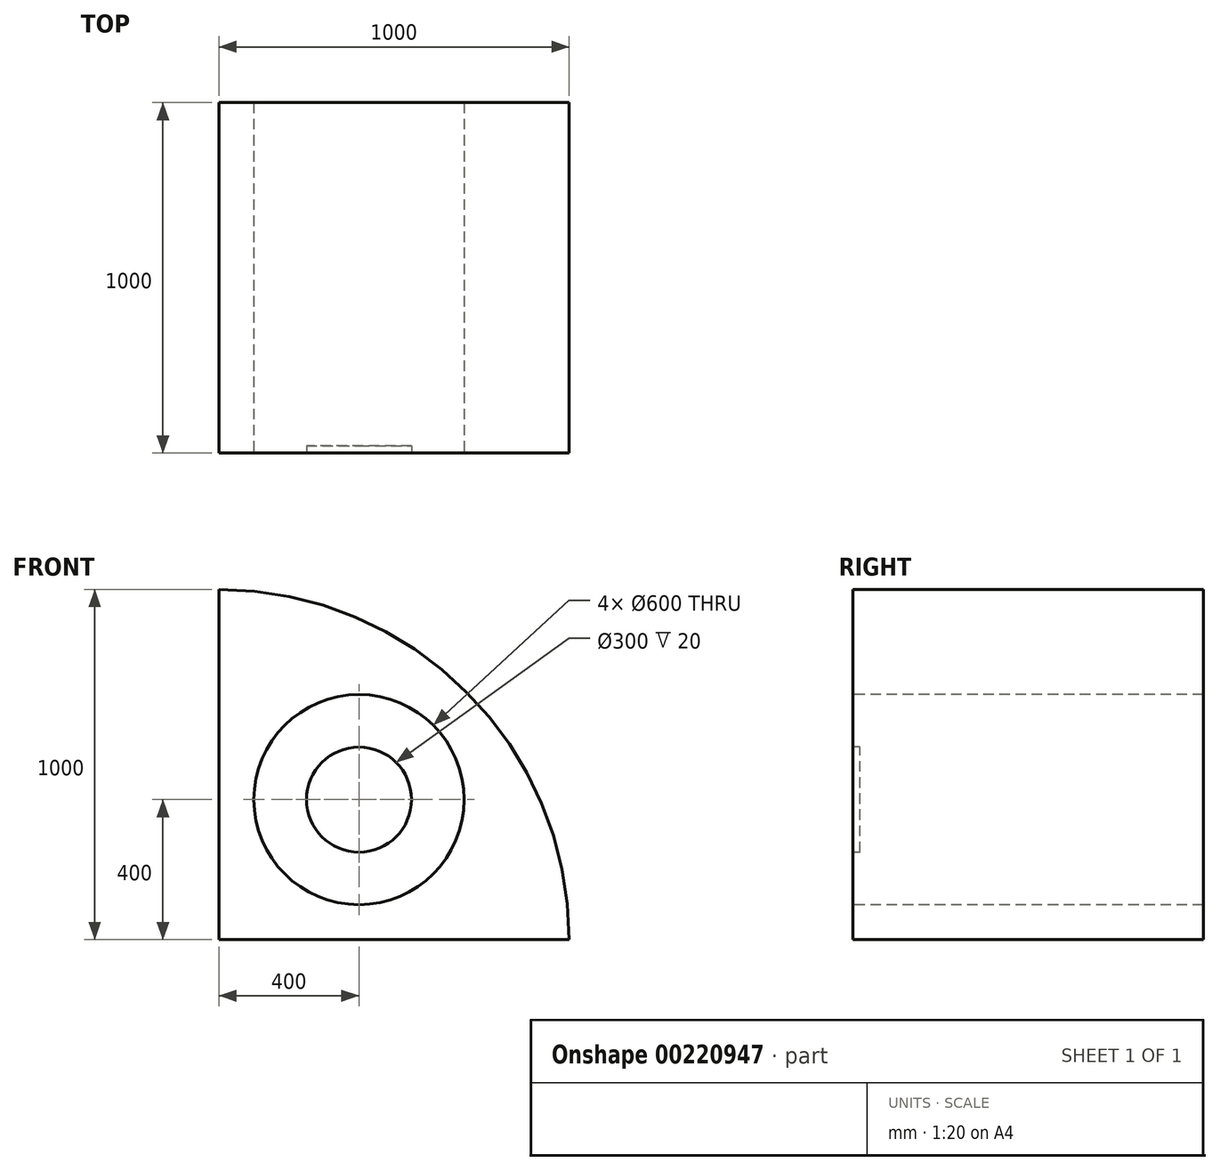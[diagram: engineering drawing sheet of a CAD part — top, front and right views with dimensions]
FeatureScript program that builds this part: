
annotation { "Feature Type Name" : "Feature", "Feature Type Description" : "" }
export const myFeature = defineFeature(function(context is Context, id is Id, definition is map)
    precondition{}
    {
        {
            var Q0;
            Q0=qCreatedBy(makeId("Front.planeOp"),FACE);
            var sketch = newSketch(context, id + "F0", { "sketchPlane" : qUnion([Q0])});
            skLineSegment(sketch, "E0", {"start": v(0, 1265.17) * mm, "end": v(0, -1140.87) * mm, "construction": true});
            skLineSegment(sketch, "E1", {"start": v(-1696.9, 0) * mm, "end": v(1278.35, 0) * mm, "construction": true});
            skArc(sketch, "E2", {"start": v(1000, 0) * mm, "mid": v(707.1, 707.1) * mm, "end": v(0, 1000) * mm});
            skLineSegment(sketch, "E3", {"start": v(0, 1000) * mm, "end": v(0, 0) * mm});
            skLineSegment(sketch, "E4", {"start": v(1000, 0) * mm, "end": v(0, 0) * mm});
            skSolve(sketch);
        }
        {
            var Q0;
            Q0=qCreatedBy(makeId("Front.planeOp"),FACE);
            var sketch = newSketch(context, id + "F1", { "sketchPlane" : qUnion([Q0])});
            skLineSegment(sketch, "E5", {"start": v(-1713.62, 0) * mm, "end": v(2054.63, 0) * mm, "construction": true});
            skLineSegment(sketch, "E6", {"start": v(0, -1617.72) * mm, "end": v(0, 1675.94) * mm, "construction": true});
            skCircle(sketch, "E7", {"center": v(-400, 400) * mm, "radius": 150 * mm, "construction": true});
            skCircle(sketch, "E8.0.1.0", {"center": v(-400, -400) * mm, "radius": 150 * mm, "construction": true});
            skCircle(sketch, "E8.1.0.0", {"center": v(400, 400) * mm, "radius": 150 * mm});
            skCircle(sketch, "E8.1.1.0", {"center": v(400, -400) * mm, "radius": 150 * mm, "construction": true});
            skLineSegment(sketch, "E8.direction1", {"start": v(-400, 400) * mm, "end": v(400, 400) * mm, "construction": true});
            skLineSegment(sketch, "E8.direction2", {"start": v(-400, 400) * mm, "end": v(-400, -400) * mm, "construction": true});
            skSolve(sketch);
        }
        {
            var Q0;
            Q0=qCreatedBy(makeId("Front.planeOp"),FACE);
            var sketch = newSketch(context, id + "F2", { "sketchPlane" : qUnion([Q0])});
            skCircle(sketch, "E9", {"center": v(400, 400) * mm, "radius": 300 * mm});
            skSolve(sketch);
        }
        {
            var Q0;
            Q0=qSketchRegion(id+"F0",true);
            extrude(context, id + "F3", {"entities" : qUnion([Q0]), "oppositeDirection" : true, "depth" : 1000 * mm});
        }
        {
            var Q0;
            Q0=makeQuery(id+"F2.imprint","IMPRINT",FACE,{"disambiguationData":[TD([[makeQuery(id+"F2.imprint","IMPRINT",EDGE,{"derivedFrom":sQuery(id+"F2.wireOp",EDGE,"E9")}),1.0]])]});
            extrude(context, id + "F4", {"entities" : qUnion([Q0]), "operationType" : NewBodyOperationType.REMOVE, "oppositeDirection" : true, "depth" : 1200 * mm});
        }
        {
            var Q0;
            Q0 = qSketchRegion(id + "F2", true);
            var Q1;
            Q1=makeQuery(id+"F3.opExtrude","CAP_FACE",FACE,{"disambiguationData":[OSD([sQuery(id+"F0.wireOp",EDGE,"E2"),sQuery(id+"F0.wireOp",EDGE,"E3"),sQuery(id+"F0.wireOp",EDGE,"E4")])],"isStart":false});
            extrude(context, id + "F5", {"entities" : qUnion([Q0]), "endBound" : BoundingType.UP_TO_SURFACE, "oppositeDirection" : true, "endBoundEntityFace" : qUnion([Q1]), "depth" : 120 * mm});
        }
        {
            var Q0;
            Q0 = qSketchRegion(id + "F1", true);
            extrude(context, id + "F6", {"entities" : qUnion([Q0]), "operationType" : NewBodyOperationType.REMOVE, "oppositeDirection" : true, "depth" : 20 * mm});
        }
    });
